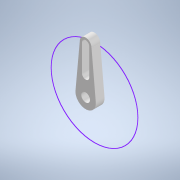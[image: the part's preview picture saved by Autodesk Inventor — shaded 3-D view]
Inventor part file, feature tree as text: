
AUTODESK INVENTOR PART (.ipt)
format: ipt  version: 2022 (Build 260153000, 153)  size: 145,408 bytes
history: native  units: mm
features: reference x8, other x7, sketch x2, extrude x1, projected_geometry x1
ambient origin geometry x8: Origin, YZ Plane, XZ Plane, XY Plane, X Axis, Y Axis, Z Axis, Center Point
bodies: Body1 (feature_tree)
feature tree (19):
  other  "Твердое тело1"
  extrude  "Выдавливание1"  Depth=4.0mm
  sketch  "Эскиз2"
  sketch  "Эскиз1"
  reference  "Ссылка1"
  reference  "Ссылка2"
  reference  "Ссылка3"
  reference  "Ссылка4"
  reference  "Ссылка5"
  projected_geometry  "Спроецированная петля1"
  reference  "Ссылка6"
  reference  "Ссылка7"
  reference  "Ссылка8"
  other  "<userpath>\Documents\Git\MZCAT_2024\MZCAT_2.iam"
  other  "MZCAT_2.iam"
  other  "OCS-D008 B:3"
  other  "lidar_base:1"
  other  "stabilisator_plan:1"
  other  "lidar_krestovina:1"
